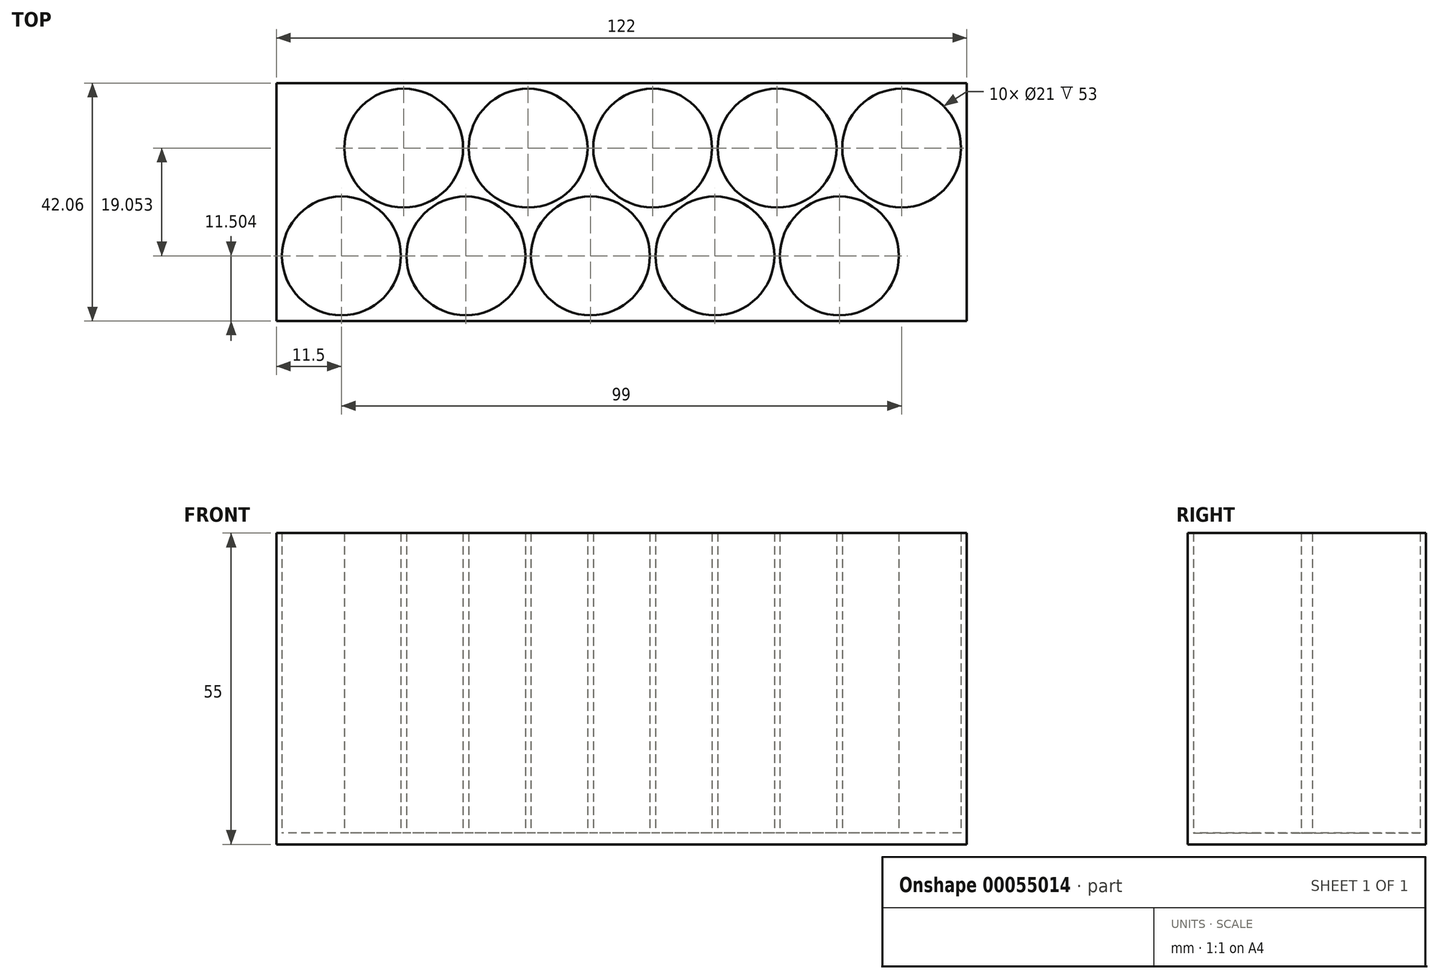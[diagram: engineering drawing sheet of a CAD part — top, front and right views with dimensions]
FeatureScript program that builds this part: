
annotation { "Feature Type Name" : "Feature", "Feature Type Description" : "" }
export const myFeature = defineFeature(function(context is Context, id is Id, definition is map)
    precondition{}
    {
        {
            var Q0;
            Q0=qCreatedBy(makeId("Top.planeOp"),FACE);
            var sketch = newSketch(context, id + "F0", { "sketchPlane" : qUnion([Q0])});
            skLineSegment(sketch, "E0.bottom", {"start": v(61, 21.03) * mm, "end": v(-61, 21.03) * mm});
            skLineSegment(sketch, "E0.top", {"start": v(61, -21.03) * mm, "end": v(-61, -21.03) * mm});
            skLineSegment(sketch, "E0.left", {"start": v(61, 21.03) * mm, "end": v(61, -21.03) * mm});
            skLineSegment(sketch, "E0.right", {"start": v(-61, 21.03) * mm, "end": v(-61, -21.03) * mm});
            skPoint(sketch, "E0.middle", {"position": v(0, 0) * mm});
            skCircle(sketch, "E1", {"center": v(-49.5, -9.53) * mm, "radius": 10.5 * mm});
            skCircle(sketch, "E2.0.1.0", {"center": v(-38.5, 9.53) * mm, "radius": 10.5 * mm});
            skCircle(sketch, "E2.1.0.0", {"center": v(-27.5, -9.53) * mm, "radius": 10.5 * mm});
            skCircle(sketch, "E2.1.1.0", {"center": v(-16.5, 9.53) * mm, "radius": 10.5 * mm});
            skCircle(sketch, "E2.2.0.0", {"center": v(-5.5, -9.53) * mm, "radius": 10.5 * mm});
            skCircle(sketch, "E2.2.1.0", {"center": v(5.5, 9.53) * mm, "radius": 10.5 * mm});
            skCircle(sketch, "E2.3.0.0", {"center": v(16.5, -9.53) * mm, "radius": 10.5 * mm});
            skCircle(sketch, "E2.3.1.0", {"center": v(27.5, 9.53) * mm, "radius": 10.5 * mm});
            skCircle(sketch, "E2.4.0.0", {"center": v(38.5, -9.53) * mm, "radius": 10.5 * mm});
            skCircle(sketch, "E2.4.1.0", {"center": v(49.5, 9.53) * mm, "radius": 10.5 * mm});
            skLineSegment(sketch, "E2.direction1", {"start": v(-49.5, -9.53) * mm, "end": v(-27.5, -9.53) * mm, "construction": true});
            skLineSegment(sketch, "E2.direction2", {"start": v(-49.5, -9.53) * mm, "end": v(-38.5, 9.53) * mm, "construction": true});
            skSolve(sketch);
        }
        {
            var Q0;
            Q0=makeQuery(id+"F0.imprint","IMPRINT",FACE,{"disambiguationData":[TD([[makeQuery(id+"F0.imprint","IMPRINT",EDGE,{"derivedFrom":sQuery(id+"F0.wireOp",EDGE,"E0.bottom")}),1.0]])]});
            extrude(context, id + "F1", {"entities" : qUnion([Q0]), "depth" : 55 * mm});
        }
        {
            var Q0;
            Q0=makeQuery(id+"F0.imprint","IMPRINT",FACE,{"disambiguationData":[TD([[makeQuery(id+"F0.imprint","IMPRINT",EDGE,{"derivedFrom":sQuery(id+"F0.wireOp",EDGE,"E2.0.1.0")}),1.0]])]});
            var Q1;
            Q1=makeQuery(id+"F0.imprint","IMPRINT",FACE,{"disambiguationData":[TD([[makeQuery(id+"F0.imprint","IMPRINT",EDGE,{"derivedFrom":sQuery(id+"F0.wireOp",EDGE,"E1")}),1.0]])]});
            var Q2;
            Q2=makeQuery(id+"F0.imprint","IMPRINT",FACE,{"disambiguationData":[TD([[makeQuery(id+"F0.imprint","IMPRINT",EDGE,{"derivedFrom":sQuery(id+"F0.wireOp",EDGE,"E2.1.0.0")}),1.0]])]});
            var Q3;
            Q3=makeQuery(id+"F0.imprint","IMPRINT",FACE,{"disambiguationData":[TD([[makeQuery(id+"F0.imprint","IMPRINT",EDGE,{"derivedFrom":sQuery(id+"F0.wireOp",EDGE,"E2.1.1.0")}),1.0]])]});
            var Q4;
            Q4=makeQuery(id+"F0.imprint","IMPRINT",FACE,{"disambiguationData":[TD([[makeQuery(id+"F0.imprint","IMPRINT",EDGE,{"derivedFrom":sQuery(id+"F0.wireOp",EDGE,"E2.2.0.0")}),1.0]])]});
            var Q5;
            Q5=makeQuery(id+"F0.imprint","IMPRINT",FACE,{"disambiguationData":[TD([[makeQuery(id+"F0.imprint","IMPRINT",EDGE,{"derivedFrom":sQuery(id+"F0.wireOp",EDGE,"E2.2.1.0")}),1.0]])]});
            var Q6;
            Q6=makeQuery(id+"F0.imprint","IMPRINT",FACE,{"disambiguationData":[TD([[makeQuery(id+"F0.imprint","IMPRINT",EDGE,{"derivedFrom":sQuery(id+"F0.wireOp",EDGE,"E2.3.0.0")}),1.0]])]});
            var Q7;
            Q7=makeQuery(id+"F0.imprint","IMPRINT",FACE,{"disambiguationData":[TD([[makeQuery(id+"F0.imprint","IMPRINT",EDGE,{"derivedFrom":sQuery(id+"F0.wireOp",EDGE,"E2.3.1.0")}),1.0]])]});
            var Q8;
            Q8=makeQuery(id+"F0.imprint","IMPRINT",FACE,{"disambiguationData":[TD([[makeQuery(id+"F0.imprint","IMPRINT",EDGE,{"derivedFrom":sQuery(id+"F0.wireOp",EDGE,"E2.4.0.0")}),1.0]])]});
            var Q9;
            Q9=makeQuery(id+"F0.imprint","IMPRINT",FACE,{"disambiguationData":[TD([[makeQuery(id+"F0.imprint","IMPRINT",EDGE,{"derivedFrom":sQuery(id+"F0.wireOp",EDGE,"E2.4.1.0")}),1.0]])]});
            extrude(context, id + "F2", {"entities" : qUnion([Q0, Q1, Q2, Q3, Q4, Q5, Q6, Q7, Q8, Q9]), "operationType" : NewBodyOperationType.ADD, "depth" : 2 * mm});
        }
    });
